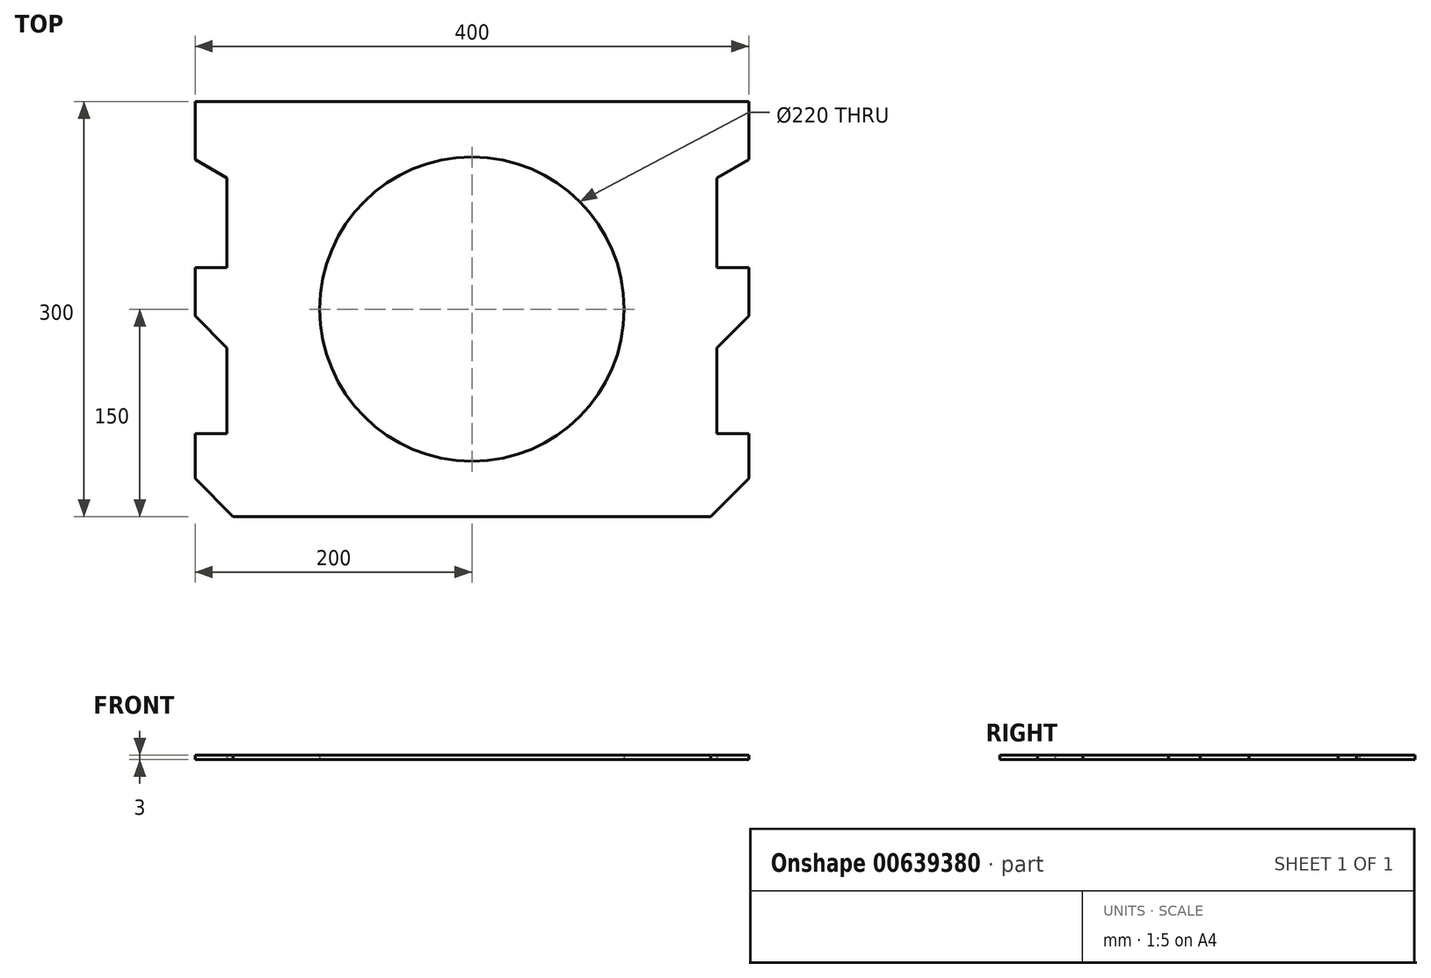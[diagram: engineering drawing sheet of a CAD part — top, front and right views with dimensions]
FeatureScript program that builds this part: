
annotation { "Feature Type Name" : "Feature", "Feature Type Description" : "" }
export const myFeature = defineFeature(function(context is Context, id is Id, definition is map)
    precondition{}
    {
        {
            var Q0;
            Q0=qCreatedBy(makeId("Top.planeOp"),FACE);
            var sketch = newSketch(context, id + "F0", { "sketchPlane" : qUnion([Q0])});
            skLineSegment(sketch, "E0.bottom", {"start": v(172.53, -150) * mm, "end": v(-172.53, -150) * mm});
            skLineSegment(sketch, "E0.top", {"start": v(200, 150) * mm, "end": v(-200, 150) * mm});
            skLineSegment(sketch, "E0.right", {"start": v(-200, -122.53) * mm, "end": v(-200, -90) * mm});
            skPoint(sketch, "E0.middle", {"position": v(0, 0) * mm});
            skLineSegment(sketch, "E1", {"start": v(-200, 108) * mm, "end": v(-177, 94.72) * mm});
            skLineSegment(sketch, "E2", {"start": v(-177, 94.72) * mm, "end": v(-177, 30) * mm});
            skLineSegment(sketch, "E3", {"start": v(-177, 30) * mm, "end": v(-200, 30) * mm});
            skLineSegment(sketch, "E4", {"start": v(-200, -5) * mm, "end": v(-177, -28) * mm});
            skLineSegment(sketch, "E5", {"start": v(-177, -90) * mm, "end": v(-200, -90) * mm});
            skLineSegment(sketch, "E6", {"start": v(-200, -122.53) * mm, "end": v(-172.53, -150) * mm});
            skLineSegment(sketch, "E7.trimOffspring", {"start": v(-200, 108) * mm, "end": v(-200, 150) * mm});
            skLineSegment(sketch, "E8", {"start": v(-177, -28) * mm, "end": v(-177, -90) * mm});
            skLineSegment(sketch, "E9.trimOffspring", {"start": v(-200, -5) * mm, "end": v(-200, 30) * mm});
            skPoint(sketch, "E10.orphan", {"position": v(-200, -150) * mm});
            skLineSegment(sketch, "E11", {"start": v(0, 150) * mm, "end": v(0, -150) * mm, "construction": true});
            skLineSegment(sketch, "E12.MirrorCS", {"start": v(200, 108) * mm, "end": v(200, 150) * mm});
            skLineSegment(sketch, "E13.MirrorCS", {"start": v(200, 108) * mm, "end": v(177, 94.72) * mm});
            skLineSegment(sketch, "E14.MirrorCS", {"start": v(177, 94.72) * mm, "end": v(177, 30) * mm});
            skLineSegment(sketch, "E15.MirrorCS", {"start": v(177, 30) * mm, "end": v(200, 30) * mm});
            skLineSegment(sketch, "E16.MirrorCS", {"start": v(200, -5) * mm, "end": v(200, 30) * mm});
            skLineSegment(sketch, "E17.MirrorCS", {"start": v(200, -5) * mm, "end": v(177, -28) * mm});
            skLineSegment(sketch, "E18.MirrorCS", {"start": v(177, -28) * mm, "end": v(177, -90) * mm});
            skLineSegment(sketch, "E19.MirrorCS", {"start": v(177, -90) * mm, "end": v(200, -90) * mm});
            skLineSegment(sketch, "E20.MirrorCS", {"start": v(200, -122.53) * mm, "end": v(200, -90) * mm});
            skLineSegment(sketch, "E21.MirrorCS", {"start": v(200, -122.53) * mm, "end": v(172.53, -150) * mm});
            skPoint(sketch, "E22.orphan", {"position": v(200, -150) * mm});
            skCircle(sketch, "E23", {"center": v(0, 0) * mm, "radius": 110 * mm});
            skCircle(sketch, "E24", {"center": v(0, 0) * mm, "radius": 120 * mm, "construction": true});
            skSolve(sketch);
        }
        {
            var Q0;
            Q0=makeQuery(id+"F0.imprint","IMPRINT",FACE,{"disambiguationData":[TD([[makeQuery(id+"F0.imprint","IMPRINT",EDGE,{"derivedFrom":sQuery(id+"F0.wireOp",EDGE,"E0.bottom")}),-1.0]])]});
            extrude(context, id + "F1", {"entities" : qUnion([Q0]), "depth" : 3 * mm, "offsetDistance" : 25 * mm});
        }
    });
